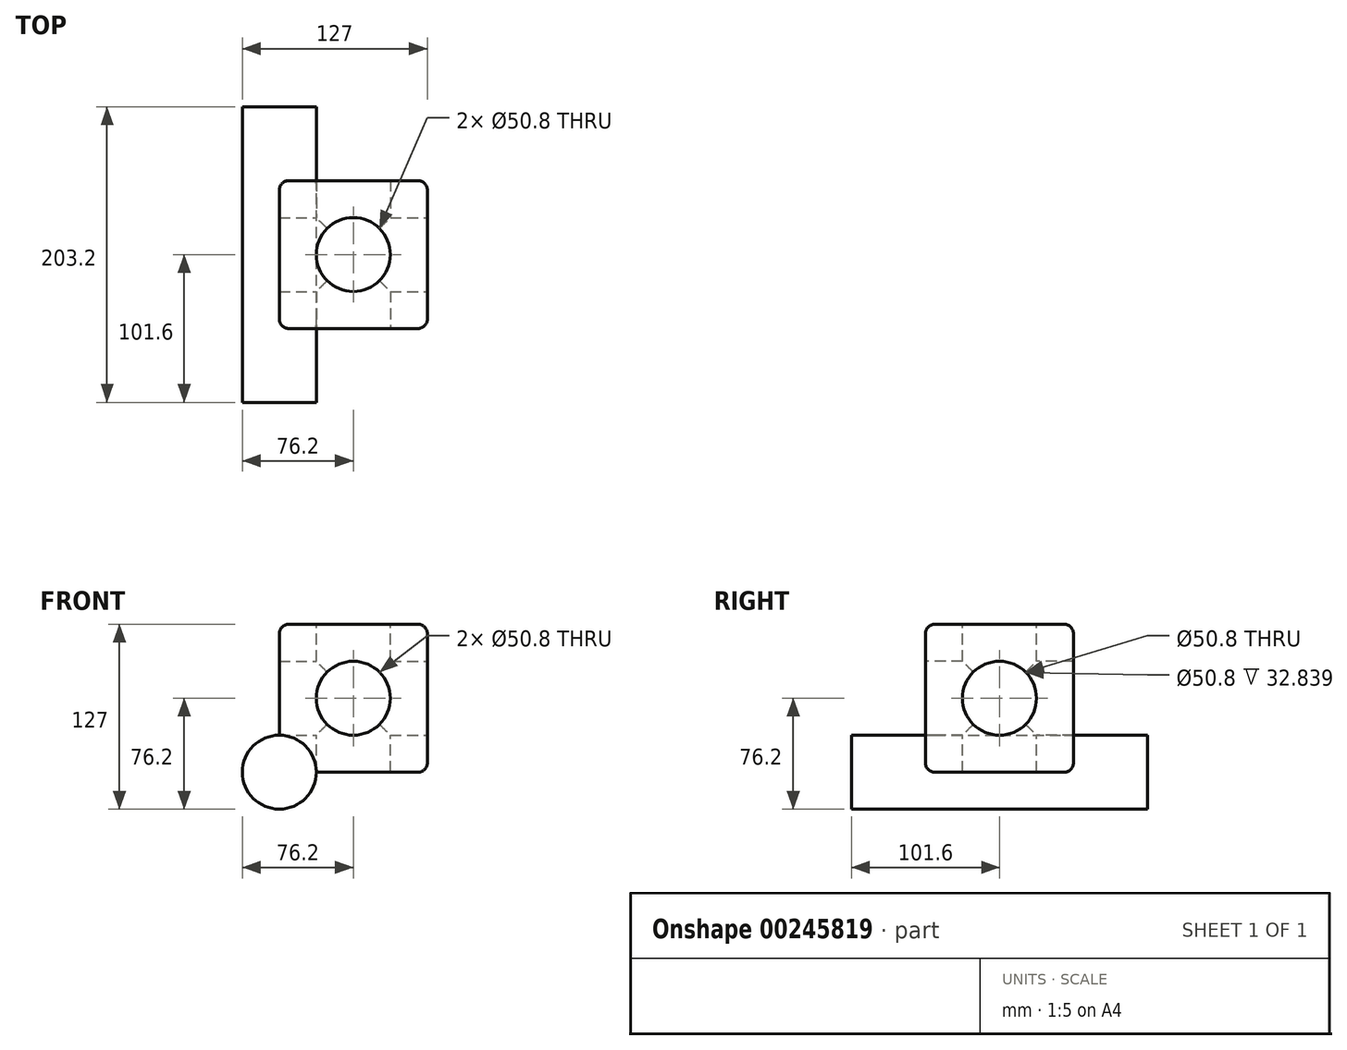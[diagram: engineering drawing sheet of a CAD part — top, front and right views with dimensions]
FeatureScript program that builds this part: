
annotation { "Feature Type Name" : "Feature", "Feature Type Description" : "" }
export const myFeature = defineFeature(function(context is Context, id is Id, definition is map)
    precondition{}
    {
        {
            var Q0;
            Q0=qCreatedBy(makeId("Front.planeOp"),FACE);
            var sketch = newSketch(context, id + "F0", { "sketchPlane" : qUnion([Q0])});
            skLineSegment(sketch, "E0", {"start": v(0, 0) * mm, "end": v(101.6, 0) * mm});
            skLineSegment(sketch, "E1", {"start": v(101.6, 0) * mm, "end": v(101.6, 101.6) * mm});
            skLineSegment(sketch, "E2", {"start": v(101.6, 101.6) * mm, "end": v(0, 101.6) * mm});
            skLineSegment(sketch, "E3", {"start": v(0, 101.6) * mm, "end": v(0, 0) * mm});
            skSolve(sketch);
        }
        {
            var Q0;
            Q0 = qSketchRegion(id + "F0", true);
            var Q1;
            Q1=makeQuery(id+"F0.imprint","IMPRINT",FACE,{"disambiguationData":[TD([[makeQuery(id+"F0.imprint","IMPRINT",EDGE,{"derivedFrom":sQuery(id+"F0.wireOp",EDGE,"E0")}),1.0]])]});
            extrude(context, id + "F1", {"entities" : qUnion([Q0, Q1]), "depth" : 101.6 * mm});
        }
        {
            var Q0;
            Q0=makeQuery(id+"F1.opExtrude","SWEPT_FACE",FACE,{"disambiguationData":[OSD([sQuery(id+"F0.wireOp",EDGE,"E2")])]});
            var sketch = newSketch(context, id + "F2", { "sketchPlane" : qUnion([Q0])});
            skCircle(sketch, "E4", {"center": v(50.8, -50.8) * mm, "radius": 25.4 * mm});
            skPoint(sketch, "E5.orphan", {"position": v(50.8, 0) * mm});
            skPoint(sketch, "E6.end.orphan", {"position": v(50.8, -101.6) * mm});
            skSolve(sketch);
        }
        {
            var Q0;
            Q0=makeQuery(id+"F2.imprint","IMPRINT",FACE,{"disambiguationData":[TD([[makeQuery(id+"F2.imprint","IMPRINT",EDGE,{"derivedFrom":sQuery(id+"F2.wireOp",EDGE,"E4")}),1.0]])]});
            extrude(context, id + "F3", {"entities" : qUnion([Q0]), "operationType" : NewBodyOperationType.REMOVE, "oppositeDirection" : true, "depth" : 101.6 * mm});
        }
        {
            var Q0;
            Q0=makeQuery(id+"F1.opExtrude","SWEPT_FACE",FACE,{"disambiguationData":[OSD([sQuery(id+"F0.wireOp",EDGE,"E1")])]});
            var sketch = newSketch(context, id + "F4", { "sketchPlane" : qUnion([Q0])});
            skCircle(sketch, "E7", {"center": v(-50.8, 50.8) * mm, "radius": 25.4 * mm});
            skPoint(sketch, "E8.orphan", {"position": v(0, 50.8) * mm});
            skPoint(sketch, "E9.end.orphan", {"position": v(-101.6, 50.8) * mm});
            skSolve(sketch);
        }
        {
            var Q0;
            Q0 = qSketchRegion(id + "F4", true);
            extrude(context, id + "F5", {"entities" : qUnion([Q0]), "operationType" : NewBodyOperationType.REMOVE, "oppositeDirection" : true, "depth" : 101.6 * mm});
        }
        {
            var Q0;
            Q0=makeQuery(id+"F1.opExtrude","CAP_FACE",FACE,{"disambiguationData":[OSD([sQuery(id+"F0.wireOp",EDGE,"E0"),sQuery(id+"F0.wireOp",EDGE,"E1"),sQuery(id+"F0.wireOp",EDGE,"E2"),sQuery(id+"F0.wireOp",EDGE,"E3")])],"isStart":false});
            var sketch = newSketch(context, id + "F6", { "sketchPlane" : qUnion([Q0])});
            skCircle(sketch, "E10", {"center": v(50.8, 50.8) * mm, "radius": 25.4 * mm});
            skPoint(sketch, "E11.orphan", {"position": v(50.8, 101.6) * mm});
            skPoint(sketch, "E12.end.orphan", {"position": v(50.8, 0) * mm});
            skSolve(sketch);
        }
        {
            var Q0;
            Q0=makeQuery(id+"F6.imprint","IMPRINT",FACE,{"disambiguationData":[TD([[makeQuery(id+"F6.imprint","IMPRINT",EDGE,{"derivedFrom":sQuery(id+"F6.wireOp",EDGE,"E10")}),1.0]])]});
            extrude(context, id + "F7", {"entities" : qUnion([Q0]), "operationType" : NewBodyOperationType.REMOVE, "oppositeDirection" : true, "depth" : 101.6 * mm});
        }
        {
            var Q0;
            Q0=makeQuery(id+"F1.opExtrude","SWEPT_EDGE",EDGE,{"disambiguationData":[OSD([sQuery(id+"F0.wireOp",EDGE,"E2"),sQuery(id+"F0.wireOp",EDGE,"E3")])]});
            var Q1;
            Q1=makeQuery(id+"F1.opExtrude","CAP_EDGE",EDGE,{"disambiguationData":[OSD([sQuery(id+"F0.wireOp",EDGE,"E2")])],"isStart":false});
            var Q2;
            Q2=makeQuery(id+"F1.opExtrude","SWEPT_EDGE",EDGE,{"disambiguationData":[OSD([sQuery(id+"F0.wireOp",EDGE,"E1"),sQuery(id+"F0.wireOp",EDGE,"E2")])]});
            var Q3;
            Q3=makeQuery(id+"F1.opExtrude","CAP_EDGE",EDGE,{"disambiguationData":[OSD([sQuery(id+"F0.wireOp",EDGE,"E2")])],"isStart":true});
            var Q4;
            Q4=makeQuery(id+"F1.opExtrude","CAP_EDGE",EDGE,{"disambiguationData":[OSD([sQuery(id+"F0.wireOp",EDGE,"E1")])],"isStart":false});
            var Q5;
            Q5=makeQuery(id+"F1.opExtrude","CAP_EDGE",EDGE,{"disambiguationData":[OSD([sQuery(id+"F0.wireOp",EDGE,"E0")])],"isStart":false});
            var Q6;
            Q6=makeQuery(id+"F1.opExtrude","CAP_EDGE",EDGE,{"disambiguationData":[OSD([sQuery(id+"F0.wireOp",EDGE,"E3")])],"isStart":false});
            var Q7;
            Q7=makeQuery(id+"F1.opExtrude","SWEPT_EDGE",EDGE,{"disambiguationData":[OSD([sQuery(id+"F0.wireOp",EDGE,"E0"),sQuery(id+"F0.wireOp",EDGE,"E1")])]});
            var Q8;
            Q8=makeQuery(id+"F1.opExtrude","CAP_EDGE",EDGE,{"disambiguationData":[OSD([sQuery(id+"F0.wireOp",EDGE,"E1")])],"isStart":true});
            var Q9;
            Q9=makeQuery(id+"F1.opExtrude","CAP_EDGE",EDGE,{"disambiguationData":[OSD([sQuery(id+"F0.wireOp",EDGE,"E0")])],"isStart":true});
            var Q10;
            Q10=makeQuery(id+"F1.opExtrude","CAP_EDGE",EDGE,{"disambiguationData":[OSD([sQuery(id+"F0.wireOp",EDGE,"E3")])],"isStart":true});
            var Q11;
            Q11=makeQuery(id+"F1.opExtrude","SWEPT_EDGE",EDGE,{"disambiguationData":[OSD([sQuery(id+"F0.wireOp",EDGE,"E0"),sQuery(id+"F0.wireOp",EDGE,"E3")])]});
            fillet(context, id + "F8", {"entities" : qUnion([Q0, Q1, Q2, Q3, Q4, Q5, Q6, Q7, Q8, Q9, Q10, Q11]), "radius" : 6.35 * mm, "tangentPropagation" : true, "allowEdgeOverflow" : false});
        }
        {
            var Q0;
            Q0=qCreatedBy(makeId("Front.planeOp"),FACE);
            cPlane(context, id + "F9", {"entities" : qUnion([Q0]), "cplaneType" : CPlaneType.OFFSET, "offset" : 101.6 * mm, "width" : 152.4 * mm, "height" : 152.4 * mm});
        }
        {
            var Q0;
            Q0=qCreatedBy(id+"F9.planeOp",FACE);
            var sketch = newSketch(context, id + "F10", { "sketchPlane" : qUnion([Q0])});
            skCircle(sketch, "E13", {"center": v(0, 0) * mm, "radius": 25.4 * mm});
            skSolve(sketch);
        }
        {
            var Q0;
            Q0 = qSketchRegion(id + "F10", true);
            extrude(context, id + "F11", {"entities" : qUnion([Q0]), "operationType" : NewBodyOperationType.ADD, "depth" : 50.8 * mm, "hasSecondDirection" : true, "secondDirectionOppositeDirection" : true, "secondDirectionDepth" : 152.4 * mm});
        }
    });
